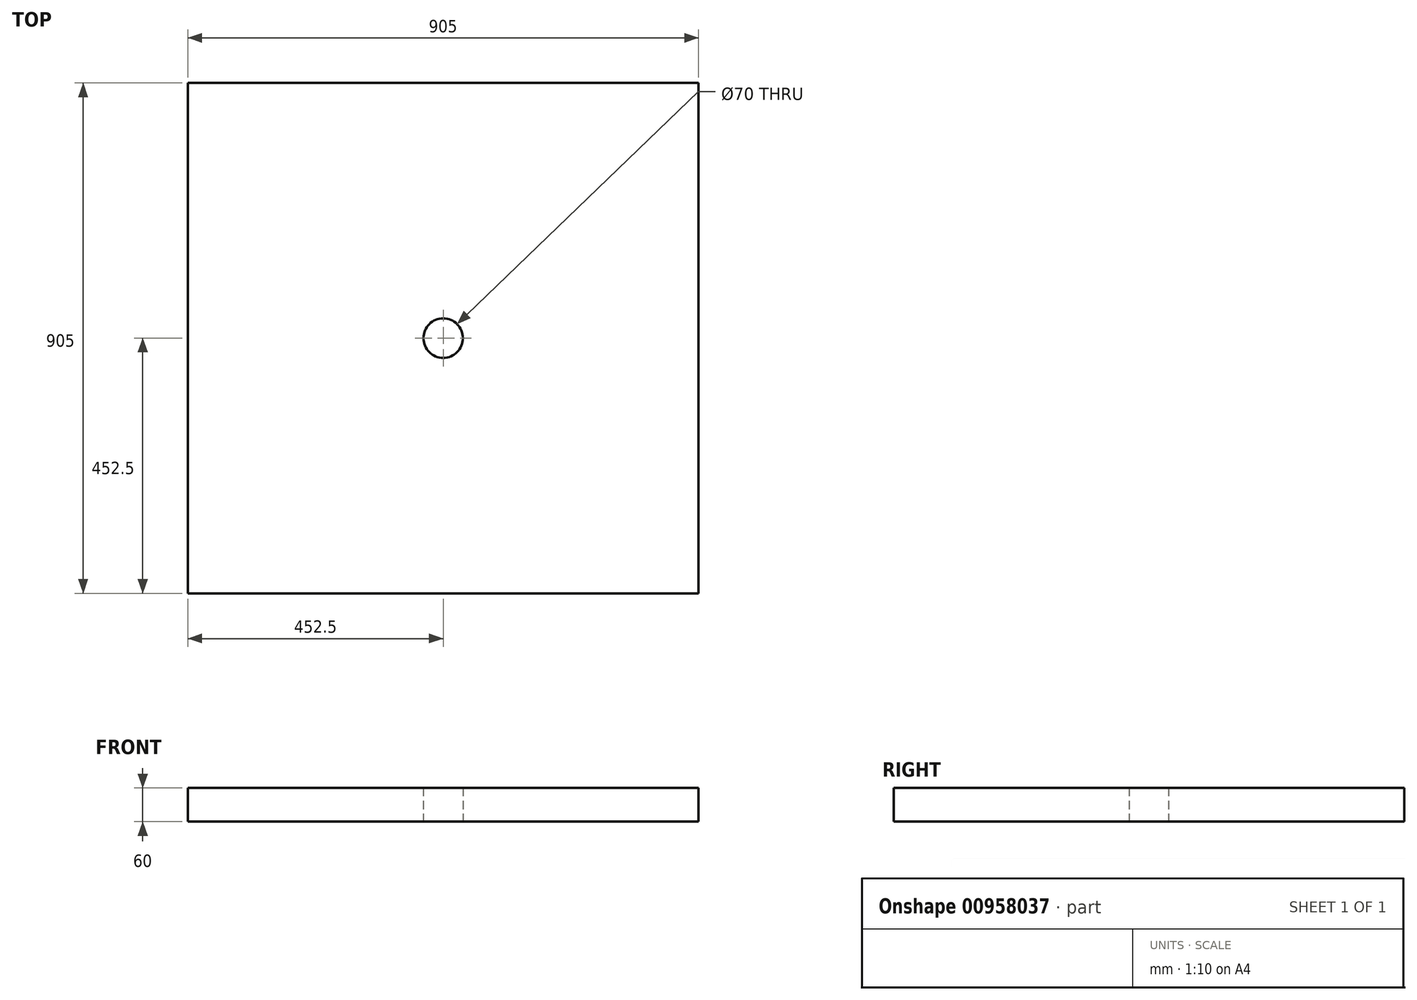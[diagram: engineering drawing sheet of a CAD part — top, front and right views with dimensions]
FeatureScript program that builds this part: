
annotation { "Feature Type Name" : "Feature", "Feature Type Description" : "" }
export const myFeature = defineFeature(function(context is Context, id is Id, definition is map)
    precondition{}
    {
        {
            var Q0;
            Q0=qCreatedBy(makeId("Top.planeOp"),FACE);
            var sketch = newSketch(context, id + "F0", { "sketchPlane" : qUnion([Q0])});
            skLineSegment(sketch, "E0.bottom", {"start": v(452.5, -452.5) * mm, "end": v(-452.5, -452.5) * mm});
            skLineSegment(sketch, "E0.top", {"start": v(452.5, 452.5) * mm, "end": v(-452.5, 452.5) * mm});
            skLineSegment(sketch, "E0.left", {"start": v(452.5, -452.5) * mm, "end": v(452.5, 452.5) * mm});
            skLineSegment(sketch, "E0.right", {"start": v(-452.5, -452.5) * mm, "end": v(-452.5, 452.5) * mm});
            skPoint(sketch, "E0.middle", {"position": v(0, 0) * mm});
            skCircle(sketch, "E1", {"center": v(0, 0) * mm, "radius": 35 * mm});
            skSolve(sketch);
        }
        {
            var Q0;
            Q0=makeQuery(id+"F0.imprint","IMPRINT",FACE,{"disambiguationData":[TD([[makeQuery(id+"F0.imprint","IMPRINT",EDGE,{"derivedFrom":sQuery(id+"F0.wireOp",EDGE,"E0.bottom")}),-1.0]])]});
            extrude(context, id + "F1", {"entities" : qUnion([Q0]), "depth" : 60 * mm, "offsetDistance" : 25 * mm});
        }
    });
